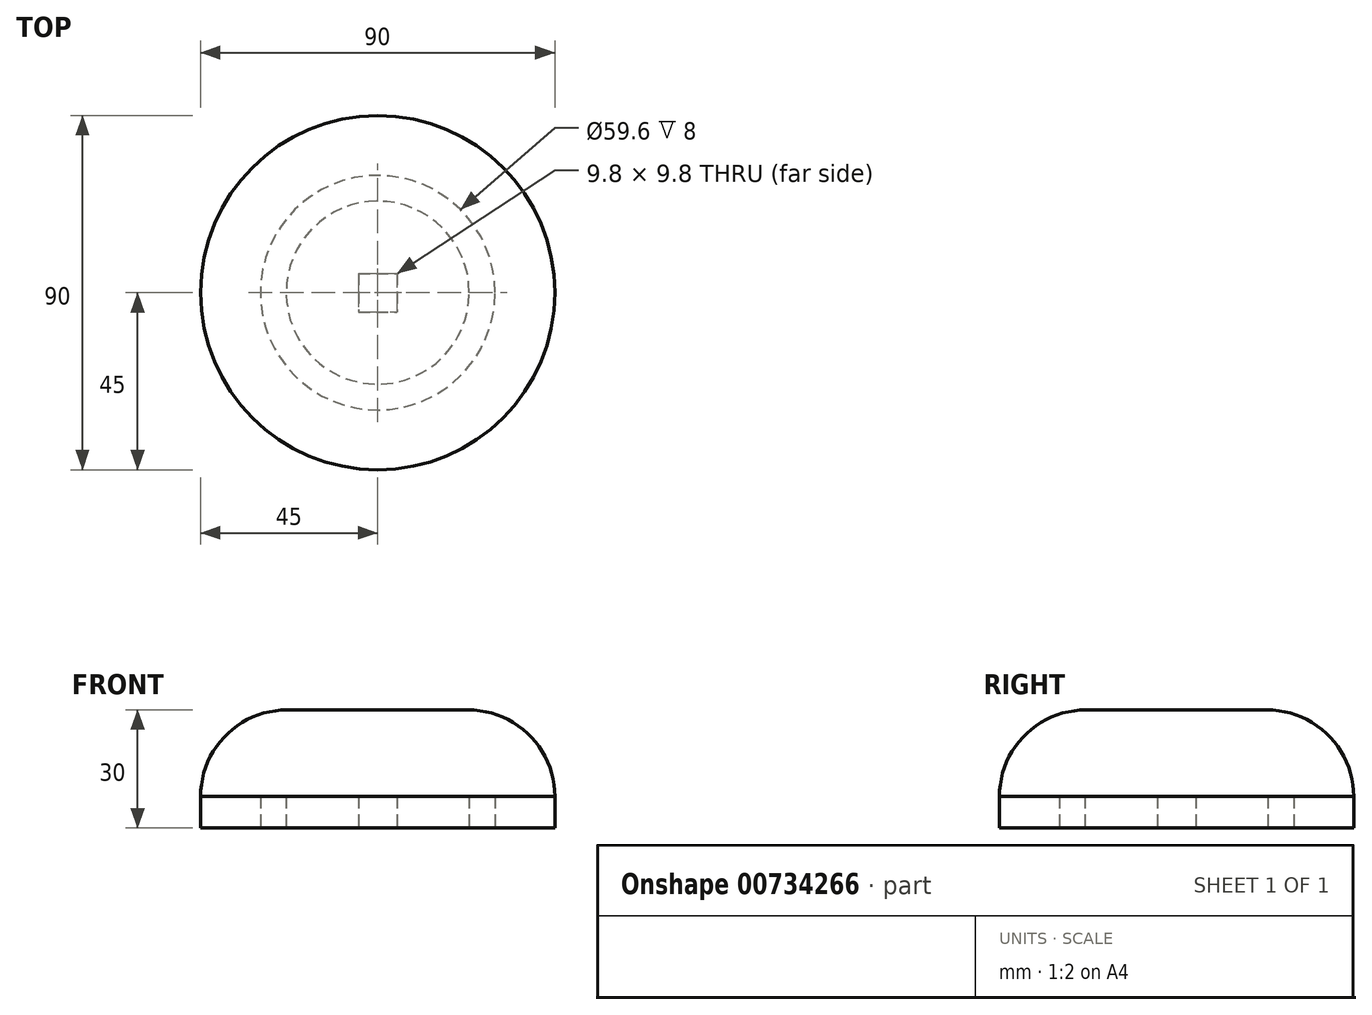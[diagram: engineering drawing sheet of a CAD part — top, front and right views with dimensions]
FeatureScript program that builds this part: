
annotation { "Feature Type Name" : "Feature", "Feature Type Description" : "" }
export const myFeature = defineFeature(function(context is Context, id is Id, definition is map)
    precondition{}
    {
        {
            var Q0;
            Q0=qCreatedBy(makeId("Top.planeOp"),FACE);
            var sketch = newSketch(context, id + "F0", { "sketchPlane" : qUnion([Q0])});
            skLineSegment(sketch, "E0.bottom", {"start": v(-4.9, 4.9) * mm, "end": v(4.9, 4.9) * mm});
            skLineSegment(sketch, "E0.top", {"start": v(-4.9, -4.9) * mm, "end": v(4.9, -4.9) * mm});
            skLineSegment(sketch, "E0.left", {"start": v(-4.9, 4.9) * mm, "end": v(-4.9, -4.9) * mm});
            skLineSegment(sketch, "E0.right", {"start": v(4.9, 4.9) * mm, "end": v(4.9, -4.9) * mm});
            skPoint(sketch, "E0.middle", {"position": v(0, 0) * mm});
            skCircle(sketch, "E1", {"center": v(0, 0) * mm, "radius": 23.25 * mm});
            skCircle(sketch, "E2", {"center": v(0, 0) * mm, "radius": 29.8 * mm});
            skCircle(sketch, "E3", {"center": v(0, 0) * mm, "radius": 45 * mm});
            skSolve(sketch);
        }
        {
            var Q0;
            Q0=makeQuery(id+"F0.imprint","IMPRINT",FACE,{"disambiguationData":[TD([[makeQuery(id+"F0.imprint","IMPRINT",EDGE,{"derivedFrom":sQuery(id+"F0.wireOp",EDGE,"E0.bottom")}),1.0]])]});
            var Q1;
            Q1=makeQuery(id+"F0.imprint","IMPRINT",FACE,{"disambiguationData":[TD([[makeQuery(id+"F0.imprint","IMPRINT",EDGE,{"derivedFrom":sQuery(id+"F0.wireOp",EDGE,"E2")}),-1.0]])]});
            extrude(context, id + "F1", {"entities" : qUnion([Q0, Q1]), "depth" : 8 * mm, "offsetDistance" : 25 * mm});
        }
        {
            var Q0;
            Q0=makeQuery(id+"F1.opExtrude","CAP_FACE",FACE,{"disambiguationData":[OSD([sQuery(id+"F0.wireOp",EDGE,"E2"),sQuery(id+"F0.wireOp",EDGE,"E3")])],"isStart":false});
            var sketch = newSketch(context, id + "F2", { "sketchPlane" : qUnion([Q0])});
            skCircle(sketch, "E4", {"center": v(0, 0) * mm, "radius": 45 * mm});
            skSolve(sketch);
        }
        {
            var Q0;
            Q0=makeQuery(id+"F2.imprint","IMPRINT",FACE,{"disambiguationData":[TD([[makeQuery(id+"F2.imprint","IMPRINT",EDGE,{"derivedFrom":sQuery(id+"F2.wireOp",EDGE,"E4")}),1.0]])]});
            var Q1;
            Q1=makeQuery(id+"F2.imprint","IMPRINT",FACE,{"disambiguationData":[TD([[makeQuery(id+"F2.imprint","IMPRINT",EDGE,{"derivedFrom":makeQuery(id+"F1.opExtrude","CAP_EDGE",EDGE,{"disambiguationData":[OSD([sQuery(id+"F0.wireOp",EDGE,"E2")])],"isStart":false})}),1.0]])]});
            extrude(context, id + "F3", {"entities" : qUnion([Q0, Q1]), "depth" : 22 * mm, "offsetDistance" : 25 * mm});
        }
        {
            var Q0;
            Q0=makeQuery(id+"F3.opExtrude","CAP_EDGE",EDGE,{"disambiguationData":[OSD([sQuery(id+"F2.wireOp",EDGE,"E4")])],"isStart":false});
            fillet(context, id + "F4", {"entities" : qUnion([Q0]), "radius" : 22 * mm, "tangentPropagation" : true, "allowEdgeOverflow" : false});
        }
    });
